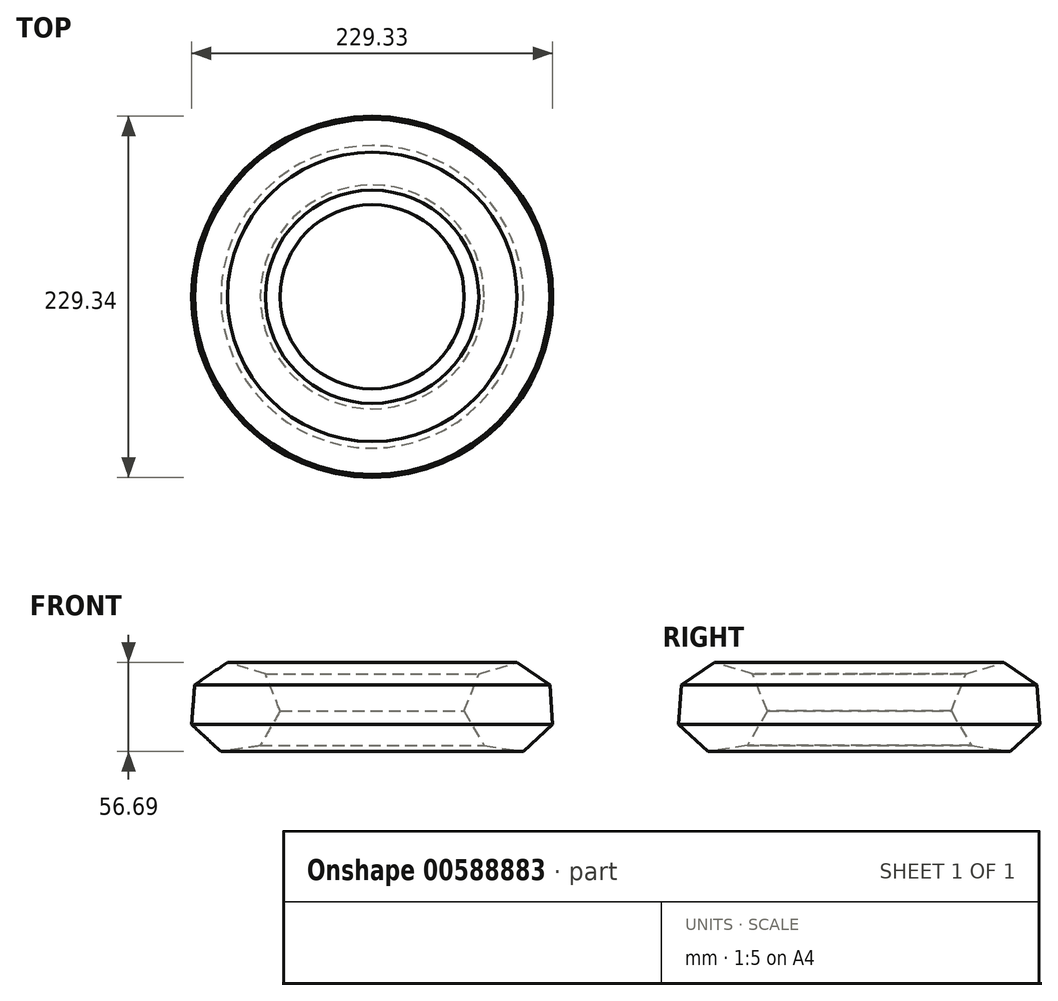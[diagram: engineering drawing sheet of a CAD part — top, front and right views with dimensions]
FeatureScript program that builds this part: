
annotation { "Feature Type Name" : "Feature", "Feature Type Description" : "" }
export const myFeature = defineFeature(function(context is Context, id is Id, definition is map)
    precondition{}
    {
        {
            var Q0;
            Q0=qCreatedBy(makeId("Front.planeOp"),FACE);
            var sketch = newSketch(context, id + "F0", { "sketchPlane" : qUnion([Q0])});
            skCircle(sketch, "E0.cCircle", {"center": v(-101.32, 28.3) * mm, "radius": 26.27 * mm, "construction": true});
            skLineSegment(sketch, "E0.0", {"start": v(-72.24, 26.14) * mm, "end": v(-84.88, 4.22) * mm});
            skLineSegment(sketch, "E0.1", {"start": v(-84.88, 4.22) * mm, "end": v(-109.9, 0.44) * mm});
            skLineSegment(sketch, "E0.2", {"start": v(-109.9, 0.44) * mm, "end": v(-128.45, 17.64) * mm});
            skLineSegment(sketch, "E0.3", {"start": v(-128.45, 17.64) * mm, "end": v(-126.58, 42.87) * mm});
            skLineSegment(sketch, "E0.4", {"start": v(-126.58, 42.87) * mm, "end": v(-105.68, 57.13) * mm});
            skLineSegment(sketch, "E0.5", {"start": v(-105.68, 57.13) * mm, "end": v(-81.5, 49.69) * mm});
            skLineSegment(sketch, "E0.6", {"start": v(-81.5, 49.69) * mm, "end": v(-72.24, 26.14) * mm});
            skPoint(sketch, "E0.0.midPoint", {"position": v(-78.56, 15.18) * mm});
            skLineSegment(sketch, "E1", {"start": v(-13.79, -28.7) * mm, "end": v(-13.79, 80.83) * mm, "construction": true});
            skSolve(sketch);
        }
        {
            var Q0;
            Q0=makeQuery(id+"F0.imprint","IMPRINT",FACE,{"disambiguationData":[TD([[makeQuery(id+"F0.imprint","IMPRINT",EDGE,{"derivedFrom":sQuery(id+"F0.wireOp",EDGE,"E0.0")}),-1.0]])]});
            var Q1;
            Q1=sQuery(id+"F0.wireOp",EDGE,"E1");
            revolve(context, id + "F1", {"entities" : qUnion([Q0]), "axis" : qUnion([Q1]), "revolveType" : RevolveType.FULL});
        }
    });
